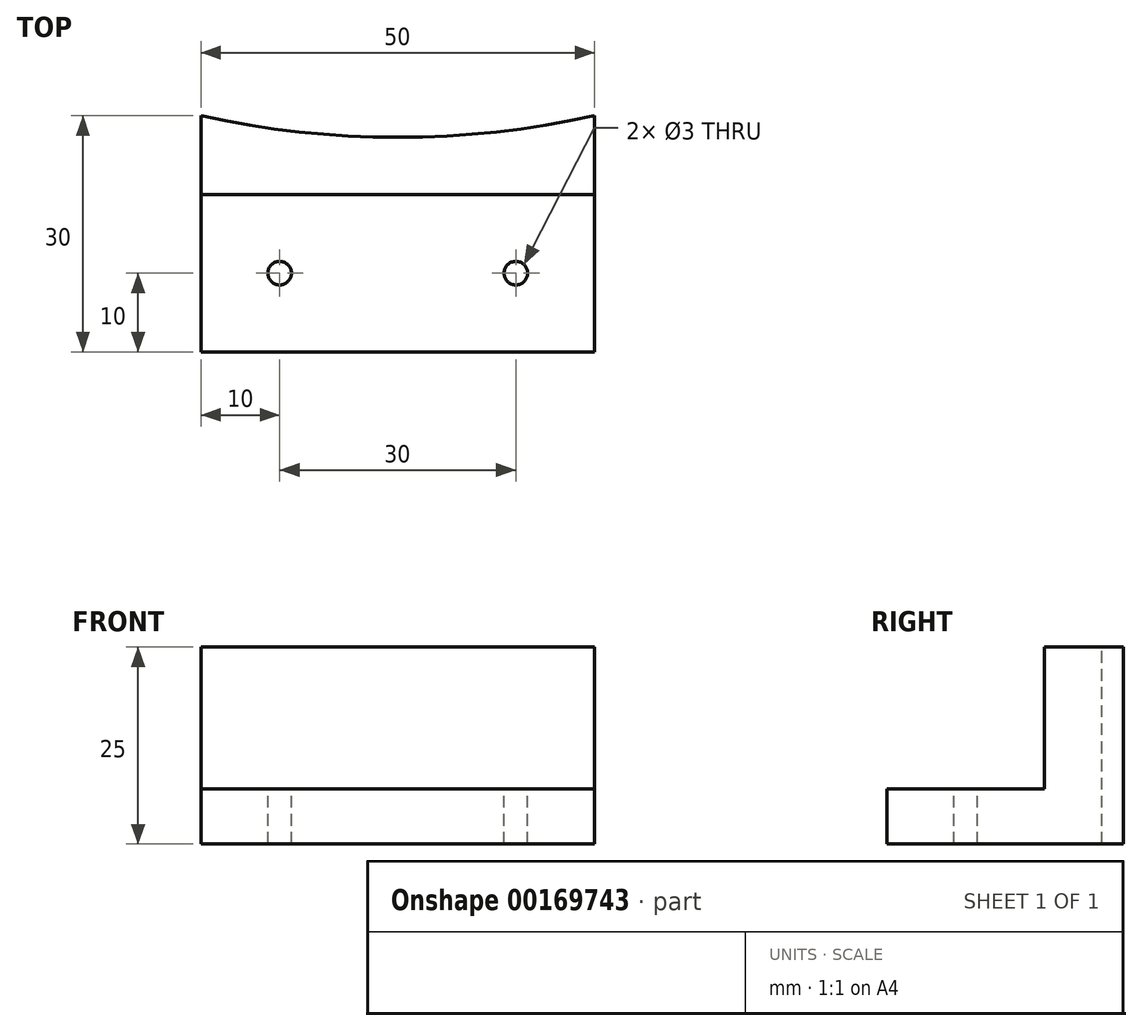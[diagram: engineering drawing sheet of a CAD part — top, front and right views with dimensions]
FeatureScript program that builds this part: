
annotation { "Feature Type Name" : "Feature", "Feature Type Description" : "" }
export const myFeature = defineFeature(function(context is Context, id is Id, definition is map)
    precondition{}
    {
        {
            var Q0;
            Q0=qCreatedBy(makeId("Top.planeOp"),FACE);
            var sketch = newSketch(context, id + "F0", { "sketchPlane" : qUnion([Q0])});
            skLineSegment(sketch, "E0.bottom", {"start": v(25, 15) * mm, "end": v(-25, 15) * mm});
            skLineSegment(sketch, "E0.top", {"start": v(25, -15) * mm, "end": v(-25, -15) * mm});
            skLineSegment(sketch, "E0.left", {"start": v(25, 15) * mm, "end": v(25, -15) * mm});
            skLineSegment(sketch, "E0.right", {"start": v(-25, 15) * mm, "end": v(-25, -15) * mm});
            skPoint(sketch, "E0.middle", {"position": v(0, 0) * mm});
            skSolve(sketch);
        }
        {
            var Q0;
            Q0=makeQuery(id+"F0.imprint","IMPRINT",FACE,{"disambiguationData":[TD([[makeQuery(id+"F0.imprint","IMPRINT",EDGE,{"derivedFrom":sQuery(id+"F0.wireOp",EDGE,"E0.bottom")}),1.0]])]});
            extrude(context, id + "F1", {"entities" : qUnion([Q0]), "depth" : 25 * mm});
        }
        {
            var Q0;
            Q0=makeQuery(id+"F1.opExtrude","CAP_FACE",FACE,{"disambiguationData":[OSD([sQuery(id+"F0.wireOp",EDGE,"E0.bottom"),sQuery(id+"F0.wireOp",EDGE,"E0.top"),sQuery(id+"F0.wireOp",EDGE,"E0.left"),sQuery(id+"F0.wireOp",EDGE,"E0.right")])],"isStart":false});
            var sketch = newSketch(context, id + "F2", { "sketchPlane" : qUnion([Q0])});
            skCircle(sketch, "E1", {"center": v(0, 127.25) * mm, "radius": 115 * mm});
            skSolve(sketch);
        }
        {
            var Q0;
            {var subQ1=makeQuery(id+"F1.opExtrude","CAP_EDGE",EDGE,{"disambiguationData":[OSD([sQuery(id+"F0.wireOp",EDGE,"E0.bottom")])],"isStart":false});Q0=makeQuery(id+"F2.imprint","IMPRINT",FACE,{"disambiguationData":[TD([[makeQuery(id+"F2.imprint","IMPRINT",EDGE,{"derivedFrom":subQ1}),1.0]])]});}
            extrude(context, id + "F3", {"entities" : qUnion([Q0]), "operationType" : NewBodyOperationType.REMOVE, "oppositeDirection" : true, "depth" : 25 * mm});
        }
        {
            var Q0;
            Q0=makeQuery(id+"F1.opExtrude","CAP_FACE",FACE,{"disambiguationData":[OSD([sQuery(id+"F0.wireOp",EDGE,"E0.bottom"),sQuery(id+"F0.wireOp",EDGE,"E0.top"),sQuery(id+"F0.wireOp",EDGE,"E0.left"),sQuery(id+"F0.wireOp",EDGE,"E0.right")])],"isStart":false});
            var sketch = newSketch(context, id + "F4", { "sketchPlane" : qUnion([Q0])});
            skLineSegment(sketch, "E2.bottom", {"start": v(-25, -15) * mm, "end": v(25, -15) * mm});
            skLineSegment(sketch, "E2.top", {"start": v(-25, 5) * mm, "end": v(25, 5) * mm});
            skLineSegment(sketch, "E2.left", {"start": v(-25, -15) * mm, "end": v(-25, 5) * mm});
            skLineSegment(sketch, "E2.right", {"start": v(25, -15) * mm, "end": v(25, 5) * mm});
            skSolve(sketch);
        }
        {
            var Q0;
            Q0=makeQuery(id+"F4.imprint","IMPRINT",FACE,{"disambiguationData":[TD([[makeQuery(id+"F4.imprint","IMPRINT",EDGE,{"derivedFrom":sQuery(id+"F4.wireOp",EDGE,"E2.bottom")}),-1.0]])]});
            extrude(context, id + "F5", {"entities" : qUnion([Q0]), "operationType" : NewBodyOperationType.REMOVE, "oppositeDirection" : true, "depth" : 18 * mm});
        }
        {
            var Q0;
            Q0=makeQuery(id+"F5.boolean.opBoolean","COPY",FACE,{"derivedFrom":makeQuery(id+"F5.opExtrude","CAP_FACE",FACE,{"disambiguationData":[OSD([sQuery(id+"F4.wireOp",EDGE,"E2.bottom"),sQuery(id+"F4.wireOp",EDGE,"E2.top"),sQuery(id+"F4.wireOp",EDGE,"E2.left"),sQuery(id+"F4.wireOp",EDGE,"E2.right")])],"isStart":false})});
            var sketch = newSketch(context, id + "F6", { "sketchPlane" : qUnion([Q0])});
            skCircle(sketch, "E3", {"center": v(-15, -5) * mm, "radius": 1.5 * mm});
            skPoint(sketch, "E3.centerSnap0", {"position": v(-25, -5) * mm});
            skCircle(sketch, "E4", {"center": v(15, -5) * mm, "radius": 1.5 * mm});
            skPoint(sketch, "E4.centerSnap0", {"position": v(25, -5) * mm});
            skSolve(sketch);
        }
        {
            var Q0;
            Q0=makeQuery(id+"F6.imprint","IMPRINT",FACE,{"disambiguationData":[TD([[makeQuery(id+"F6.imprint","IMPRINT",EDGE,{"derivedFrom":sQuery(id+"F6.wireOp",EDGE,"E3")}),1.0]])]});
            var Q1;
            Q1=makeQuery(id+"F6.imprint","IMPRINT",FACE,{"disambiguationData":[TD([[makeQuery(id+"F6.imprint","IMPRINT",EDGE,{"derivedFrom":sQuery(id+"F6.wireOp",EDGE,"E4")}),1.0]])]});
            extrude(context, id + "F7", {"entities" : qUnion([Q0, Q1]), "operationType" : NewBodyOperationType.REMOVE, "oppositeDirection" : true, "depth" : 25 * mm});
        }
    });
